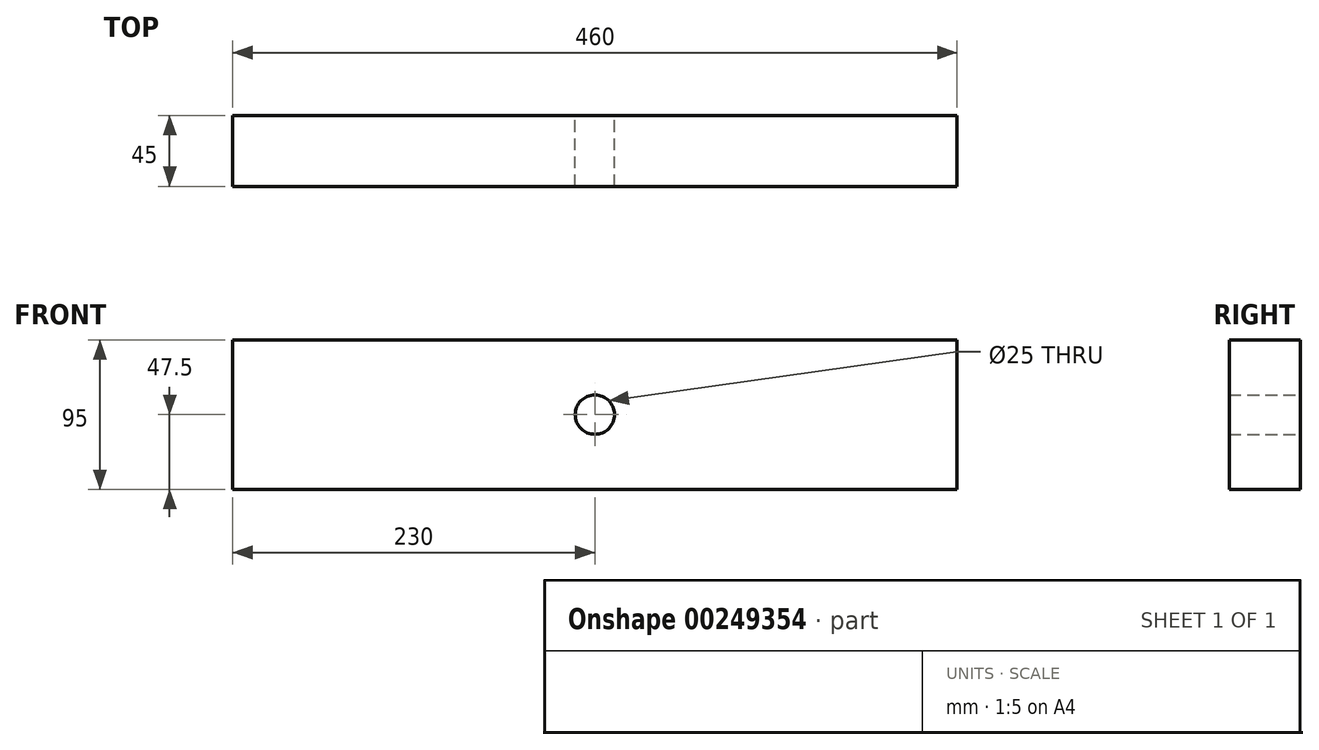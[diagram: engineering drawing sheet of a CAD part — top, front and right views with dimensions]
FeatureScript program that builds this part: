
annotation { "Feature Type Name" : "Feature", "Feature Type Description" : "" }
export const myFeature = defineFeature(function(context is Context, id is Id, definition is map)
    precondition{}
    {
        {
            var Q0;
            Q0=qCreatedBy(makeId("Front.planeOp"),FACE);
            var sketch = newSketch(context, id + "F0", { "sketchPlane" : qUnion([Q0])});
            skLineSegment(sketch, "E0.bottom", {"start": v(230, 47.5) * mm, "end": v(-230, 47.5) * mm});
            skLineSegment(sketch, "E0.top", {"start": v(230, -47.5) * mm, "end": v(-230, -47.5) * mm});
            skLineSegment(sketch, "E0.left", {"start": v(230, 47.5) * mm, "end": v(230, -47.5) * mm});
            skLineSegment(sketch, "E0.right", {"start": v(-230, 47.5) * mm, "end": v(-230, -47.5) * mm});
            skPoint(sketch, "E0.middle", {"position": v(0, 0) * mm});
            skCircle(sketch, "E1", {"center": v(0, 0) * mm, "radius": 12.5 * mm});
            skSolve(sketch);
        }
        {
            var Q0;
            Q0=makeQuery(id+"F0.imprint","IMPRINT",FACE,{"disambiguationData":[TD([[makeQuery(id+"F0.imprint","IMPRINT",EDGE,{"derivedFrom":sQuery(id+"F0.wireOp",EDGE,"E0.bottom")}),1.0]])]});
            extrude(context, id + "F1", {"entities" : qUnion([Q0]), "depth" : 45 * mm});
        }
    });
